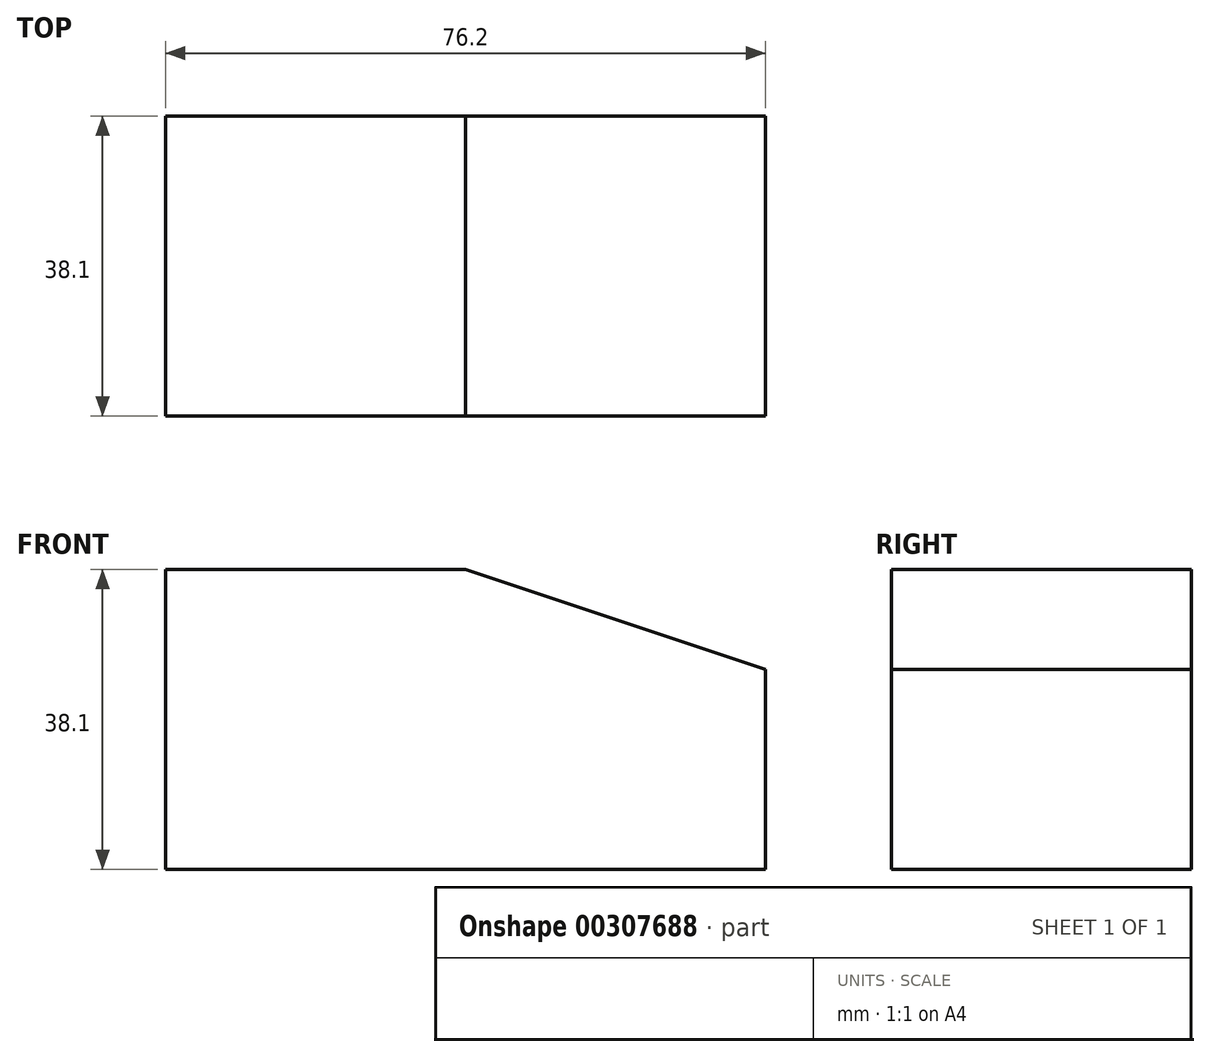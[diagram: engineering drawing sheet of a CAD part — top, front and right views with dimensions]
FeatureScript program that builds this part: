
annotation { "Feature Type Name" : "Feature", "Feature Type Description" : "" }
export const myFeature = defineFeature(function(context is Context, id is Id, definition is map)
    precondition{}
    {
        {
            var Q0;
            Q0=qCreatedBy(makeId("Front.planeOp"),FACE);
            var sketch = newSketch(context, id + "F0", { "sketchPlane" : qUnion([Q0])});
            skLineSegment(sketch, "E0", {"start": v(-34.74, -32.17) * mm, "end": v(41.46, -32.17) * mm});
            skLineSegment(sketch, "E1", {"start": v(41.46, -32.17) * mm, "end": v(41.46, -6.77) * mm});
            skLineSegment(sketch, "E2", {"start": v(-34.74, -32.17) * mm, "end": v(-34.74, 5.93) * mm});
            skLineSegment(sketch, "E3", {"start": v(-34.74, 5.93) * mm, "end": v(3.36, 5.93) * mm});
            skLineSegment(sketch, "E4", {"start": v(3.36, 5.93) * mm, "end": v(41.46, -6.77) * mm});
            skSolve(sketch);
        }
        {
            var Q0;
            Q0=makeQuery(id+"F0.imprint","IMPRINT",FACE,{"disambiguationData":[TD([[makeQuery(id+"F0.imprint","IMPRINT",EDGE,{"derivedFrom":sQuery(id+"F0.wireOp",EDGE,"E0")}),1.0]])]});
            extrude(context, id + "F1", {"entities" : qUnion([Q0]), "oppositeDirection" : true, "depth" : 38.1 * mm});
        }
    });
